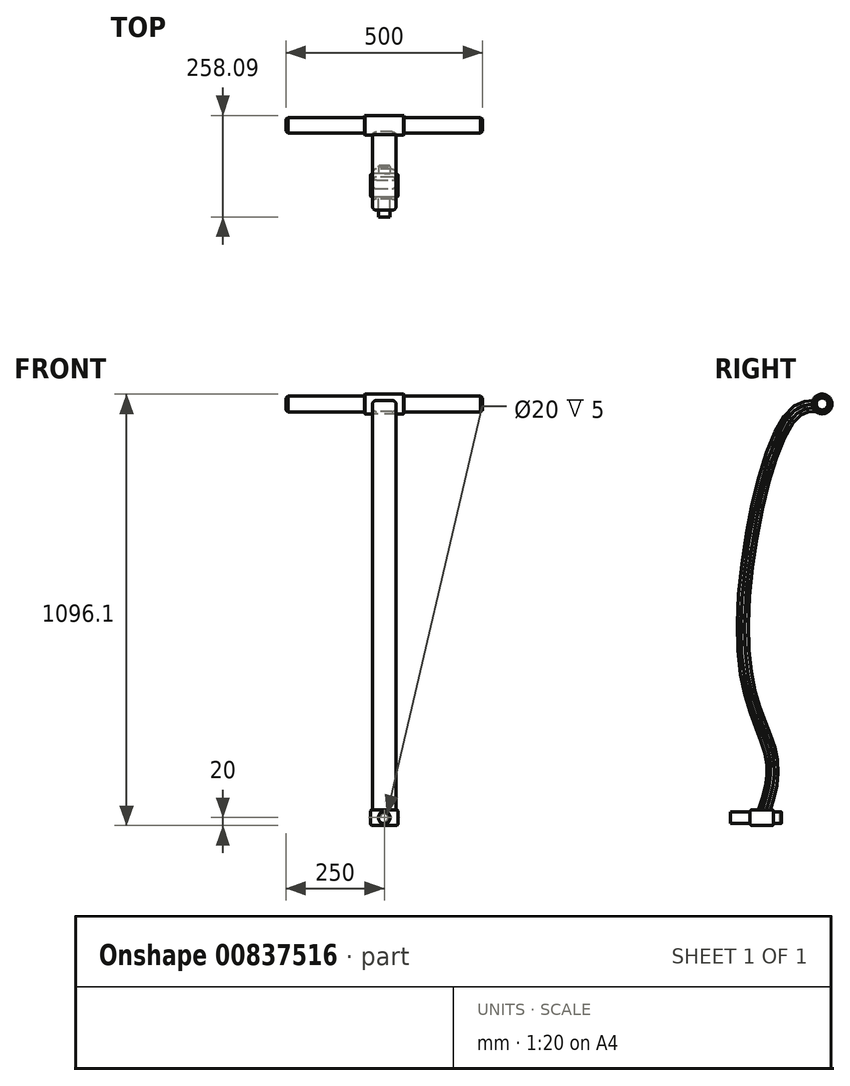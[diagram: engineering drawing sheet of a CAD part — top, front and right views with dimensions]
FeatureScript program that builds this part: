
annotation { "Feature Type Name" : "Feature", "Feature Type Description" : "" }
export const myFeature = defineFeature(function(context is Context, id is Id, definition is map)
    precondition{}
    {
        {
            var Q0;
            Q0=qCreatedBy(makeId("Top.planeOp"),FACE);
            var sketch = newSketch(context, id + "F0", { "sketchPlane" : qUnion([Q0])});
            skLineSegment(sketch, "E0.bottom", {"start": v(-20, 15) * mm, "end": v(20, 15) * mm});
            skLineSegment(sketch, "E0.top", {"start": v(-20, -15) * mm, "end": v(20, -15) * mm});
            skLineSegment(sketch, "E0.left", {"start": v(-30, 5) * mm, "end": v(-30, -5) * mm});
            skLineSegment(sketch, "E0.right", {"start": v(30, 5) * mm, "end": v(30, -5) * mm});
            skPoint(sketch, "E0.middle", {"position": v(0, 0) * mm});
            skPoint(sketch, "E1.visualSharp", {"position": v(-30, 15) * mm});
            skArc(sketch, "E1.filletArc", {"start": v(-20, 15) * mm, "mid": v(-27.07, 12.07) * mm, "end": v(-30, 5) * mm});
            skPoint(sketch, "E2.visualSharp", {"position": v(-30, -15) * mm});
            skArc(sketch, "E2.filletArc", {"start": v(-30, -5) * mm, "mid": v(-27.07, -12.07) * mm, "end": v(-20, -15) * mm});
            skPoint(sketch, "E3.visualSharp", {"position": v(30, -15) * mm});
            skArc(sketch, "E3.filletArc", {"start": v(20, -15) * mm, "mid": v(27.07, -12.07) * mm, "end": v(30, -5) * mm});
            skPoint(sketch, "E4.visualSharp", {"position": v(30, 15) * mm});
            skArc(sketch, "E4.filletArc", {"start": v(30, 5) * mm, "mid": v(27.07, 12.07) * mm, "end": v(20, 15) * mm});
            skSolve(sketch);
        }
        {
            var Q0;
            Q0=qCreatedBy(makeId("Right.planeOp"),FACE);
            var sketch = newSketch(context, id + "F1", { "sketchPlane" : qUnion([Q0])});
            skLineSegment(sketch, "E5", {"start": v(0, 0) * mm, "end": v(0, 1050) * mm, "construction": true});
            skFitSpline(sketch, "E6", {"points": [v(0, 0) * mm, v(25.89, 145.63) * mm, v(-45.25, 402.18) * mm, v(81.94, 1027.38) * mm, v(153.09, 1051.1) * mm], "startDerivative": vector(255.01, 740.87) * mm, "endDerivative": vector(407.15, 207.13) * mm});
            skSolve(sketch);
        }
        {
            var Q0;
            Q0=makeQuery(id+"F0.imprint","IMPRINT",FACE,{"disambiguationData":[TD([[makeQuery(id+"F0.imprint","IMPRINT",EDGE,{"derivedFrom":sQuery(id+"F0.wireOp",EDGE,"E0.bottom")}),-1.0]])]});
            var Q1;
            Q1=sQuery(id+"F1.wireOp",EDGE,"E6");
            sweep(context, id + "F2", {"profiles" : qUnion([Q0]), "path" : qUnion([Q1])});
        }
        {
            var Q0;
            Q0=qCreatedBy(makeId("Right.planeOp"),FACE);
            var sketch = newSketch(context, id + "F3", { "sketchPlane" : qUnion([Q0])});
            skCircle(sketch, "E7", {"center": v(153.09, 1051.1) * mm, "radius": 25 * mm});
            skSolve(sketch);
        }
        {
            var Q0;
            Q0 = qSketchRegion(id + "F3", true);
            extrude(context, id + "F4", {"entities" : qUnion([Q0]), "operationType" : NewBodyOperationType.ADD, "endBound" : BoundingType.SYMMETRIC, "depth" : 100 * mm, "offsetDistance" : 25 * mm});
        }
        {
            var Q0;
            Q0=qCreatedBy(makeId("Right.planeOp"),FACE);
            var sketch = newSketch(context, id + "F5", { "sketchPlane" : qUnion([Q0])});
            skCircle(sketch, "E8", {"center": v(153.09, 1051.1) * mm, "radius": 20 * mm});
            skSolve(sketch);
        }
        {
            var Q0;
            Q0 = qSketchRegion(id + "F5", true);
            extrude(context, id + "F6", {"entities" : qUnion([Q0]), "operationType" : NewBodyOperationType.ADD, "endBound" : BoundingType.SYMMETRIC, "depth" : 500 * mm, "offsetDistance" : 25 * mm});
        }
        {
            var Q0;
            Q0=makeQuery(id+"F6.opExtrude","CAP_EDGE",EDGE,{"disambiguationData":[OSD([sQuery(id+"F5.wireOp",EDGE,"E8")])],"isStart":true});
            var Q1;
            Q1=makeQuery(id+"F6.opExtrude","CAP_EDGE",EDGE,{"disambiguationData":[OSD([sQuery(id+"F5.wireOp",EDGE,"E8")])],"isStart":false});
            chamfer(context, id + "F7", {"entities" : qUnion([Q0, Q1]), "width" : 5 * mm, "tangentPropagation" : true});
        }
        {
            var Q0;
            Q0=qCreatedBy(makeId("Right.planeOp"),FACE);
            var sketch = newSketch(context, id + "F8", { "sketchPlane" : qUnion([Q0])});
            skLineSegment(sketch, "E9.bottom", {"start": v(30, -20) * mm, "end": v(-30, -20) * mm});
            skLineSegment(sketch, "E9.top", {"start": v(30, 20) * mm, "end": v(-30, 20) * mm});
            skLineSegment(sketch, "E9.left", {"start": v(30, -20) * mm, "end": v(30, 20) * mm});
            skLineSegment(sketch, "E9.right", {"start": v(-30, -20) * mm, "end": v(-30, 20) * mm});
            skPoint(sketch, "E9.middle", {"position": v(0, 0) * mm});
            skSolve(sketch);
        }
        {
            var Q0;
            Q0 = qSketchRegion(id + "F8", true);
            extrude(context, id + "F9", {"entities" : qUnion([Q0]), "operationType" : NewBodyOperationType.ADD, "endBound" : BoundingType.SYMMETRIC, "depth" : 70 * mm, "offsetDistance" : 25 * mm});
        }
        {
            var Q0;
            Q0=makeQuery(id+"F9.opExtrude","CAP_FACE",FACE,{"disambiguationData":[OSD([sQuery(id+"F8.wireOp",EDGE,"E9.bottom"),sQuery(id+"F8.wireOp",EDGE,"E9.top"),sQuery(id+"F8.wireOp",EDGE,"E9.left"),sQuery(id+"F8.wireOp",EDGE,"E9.right")])],"isStart":false});
            var Q1;
            Q1=makeQuery(id+"F9.opExtrude","CAP_FACE",FACE,{"disambiguationData":[OSD([sQuery(id+"F8.wireOp",EDGE,"E9.bottom"),sQuery(id+"F8.wireOp",EDGE,"E9.top"),sQuery(id+"F8.wireOp",EDGE,"E9.left"),sQuery(id+"F8.wireOp",EDGE,"E9.right")])],"isStart":true});
            var Q2;
            Q2=makeQuery(id+"F9.opExtrude","SWEPT_FACE",FACE,{"disambiguationData":[OSD([sQuery(id+"F8.wireOp",EDGE,"E9.left")])]});
            var Q3;
            Q3=makeQuery(id+"F9.opExtrude","SWEPT_FACE",FACE,{"disambiguationData":[OSD([sQuery(id+"F8.wireOp",EDGE,"E9.right")])]});
            var Q4;
            Q4=makeQuery(id+"F9.opExtrude","SWEPT_FACE",FACE,{"disambiguationData":[OSD([sQuery(id+"F8.wireOp",EDGE,"E9.bottom")])]});
            fillet(context, id + "F10", {"entities" : qUnion([Q0, Q1, Q2, Q3, Q4]), "radius" : 5 * mm, "tangentPropagation" : true, "allowEdgeOverflow" : false});
        }
        {
            var Q0;
            Q0=makeQuery(id+"F9.opExtrude","SWEPT_FACE",FACE,{"disambiguationData":[OSD([sQuery(id+"F8.wireOp",EDGE,"E9.left")])]});
            var sketch = newSketch(context, id + "F11", { "sketchPlane" : qUnion([Q0])});
            skCircle(sketch, "E10", {"center": v(0, 0) * mm, "radius": 15 * mm});
            skSolve(sketch);
        }
        {
            var Q0;
            Q0 = qSketchRegion(id + "F11", true);
            extrude(context, id + "F12", {"entities" : qUnion([Q0]), "operationType" : NewBodyOperationType.ADD, "depth" : 20 * mm, "offsetDistance" : 25 * mm});
        }
        {
            var Q0;
            Q0=makeQuery(id+"F12.opExtrude","CAP_FACE",FACE,{"disambiguationData":[OSD([sQuery(id+"F11.wireOp",EDGE,"E10")])],"isStart":false});
            var sketch = newSketch(context, id + "F13", { "sketchPlane" : qUnion([Q0])});
            skCircle(sketch, "E11", {"center": v(0, 0) * mm, "radius": 10 * mm});
            skSolve(sketch);
        }
        {
            var Q0;
            Q0 = qSketchRegion(id + "F13", true);
            extrude(context, id + "F14", {"entities" : qUnion([Q0]), "operationType" : NewBodyOperationType.REMOVE, "oppositeDirection" : true, "depth" : 5 * mm, "offsetDistance" : 25 * mm});
        }
        {
            var Q0;
            Q0=makeQuery(id+"F12.opExtrude","CAP_EDGE",EDGE,{"disambiguationData":[OSD([sQuery(id+"F11.wireOp",EDGE,"E10")])],"isStart":false});
            var Q1;
            Q1=makeQuery(id+"F14.boolean.opBoolean","COPY",EDGE,{"derivedFrom":makeQuery(id+"F14.opExtrude","CAP_EDGE",EDGE,{"disambiguationData":[OSD([sQuery(id+"F13.wireOp",EDGE,"E11")])],"isStart":true})});
            fillet(context, id + "F15", {"entities" : qUnion([Q0, Q1]), "radius" : 2 * mm, "tangentPropagation" : true, "allowEdgeOverflow" : false});
        }
        {
            var Q0;
            Q0=makeQuery(id+"F9.opExtrude","SWEPT_FACE",FACE,{"disambiguationData":[OSD([sQuery(id+"F8.wireOp",EDGE,"E9.right")])]});
            var sketch = newSketch(context, id + "F16", { "sketchPlane" : qUnion([Q0])});
            skCircle(sketch, "E12", {"center": v(0, 0) * mm, "radius": 15 * mm});
            skSolve(sketch);
        }
        {
            var Q0;
            Q0 = qSketchRegion(id + "F16", true);
            extrude(context, id + "F17", {"entities" : qUnion([Q0]), "operationType" : NewBodyOperationType.ADD, "depth" : 50 * mm, "offsetDistance" : 25 * mm});
        }
        {
            var Q0;
            Q0=makeQuery(id+"F4.opExtrude","CAP_EDGE",EDGE,{"disambiguationData":[OSD([sQuery(id+"F3.wireOp",EDGE,"E7")])],"isStart":false});
            var Q1;
            Q1=makeQuery(id+"F4.opExtrude","CAP_EDGE",EDGE,{"disambiguationData":[OSD([sQuery(id+"F3.wireOp",EDGE,"E7")])],"isStart":true});
            chamfer(context, id + "F18", {"entities" : qUnion([Q0, Q1]), "width" : 1 * mm, "tangentPropagation" : true});
        }
    });
